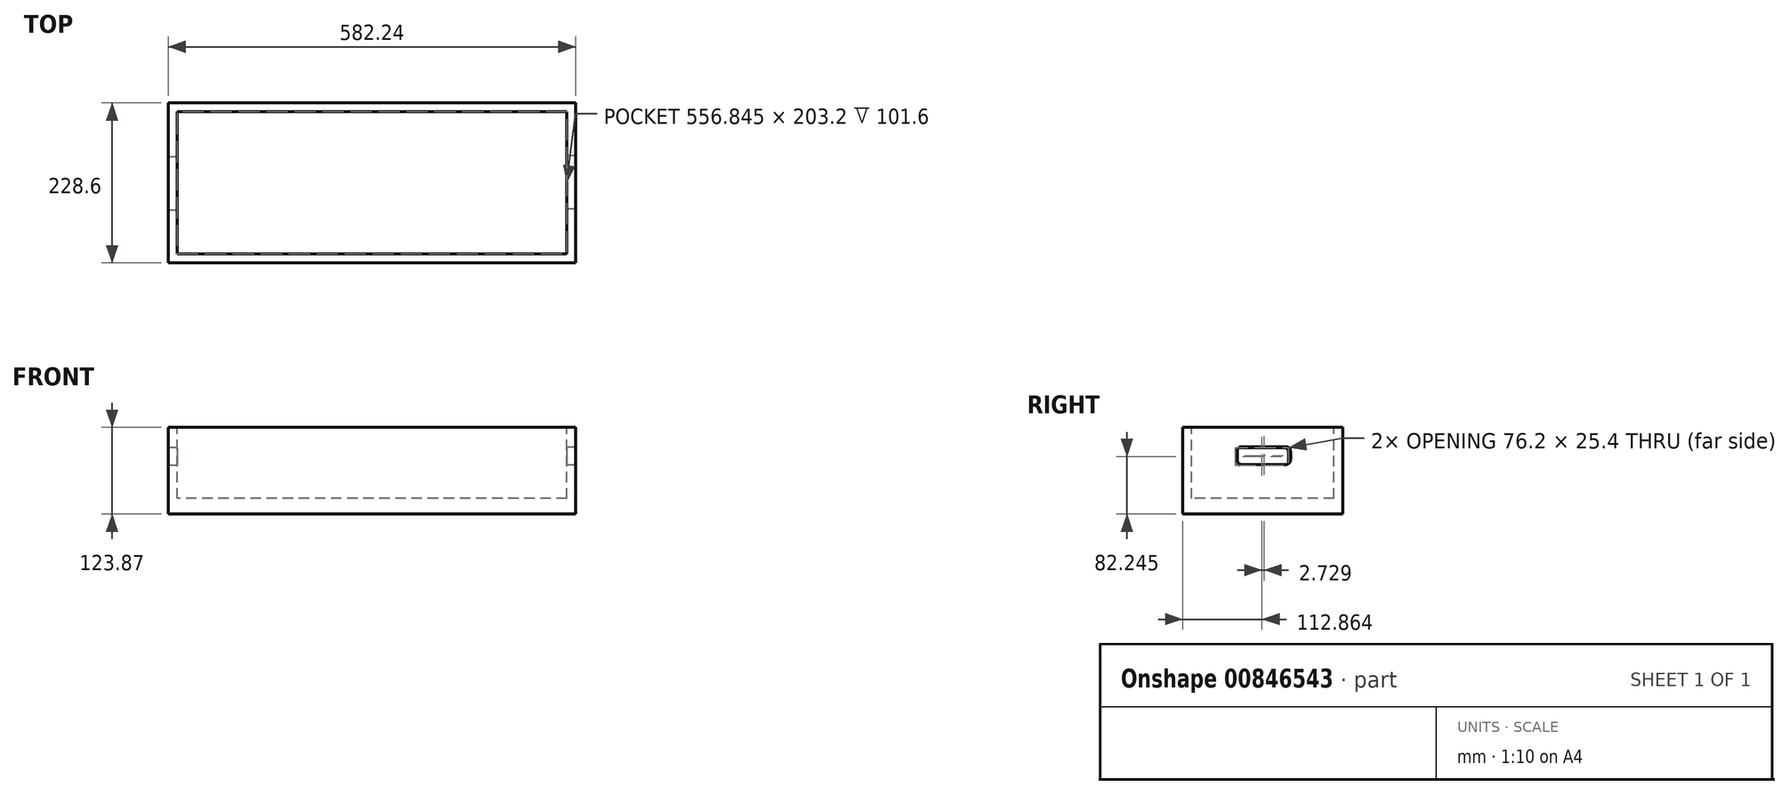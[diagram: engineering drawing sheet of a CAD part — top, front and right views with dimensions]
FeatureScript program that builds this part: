
annotation { "Feature Type Name" : "Feature", "Feature Type Description" : "" }
export const myFeature = defineFeature(function(context is Context, id is Id, definition is map)
    precondition{}
    {
        {
            var Q0;
            Q0=qCreatedBy(makeId("Front.planeOp"),FACE);
            var sketch = newSketch(context, id + "F0", { "sketchPlane" : qUnion([Q0])});
            skLineSegment(sketch, "E0.bottom", {"start": v(-103.31, 21.1) * mm, "end": v(478.93, 21.1) * mm});
            skLineSegment(sketch, "E0.top", {"start": v(-103.31, -102.77) * mm, "end": v(478.93, -102.77) * mm});
            skLineSegment(sketch, "E0.left", {"start": v(-103.31, 21.1) * mm, "end": v(-103.31, -102.77) * mm});
            skLineSegment(sketch, "E0.right", {"start": v(478.93, 21.1) * mm, "end": v(478.93, -102.77) * mm});
            skSolve(sketch);
        }
        {
            var Q0;
            Q0 = qSketchRegion(id + "F0", true);
            extrude(context, id + "F1", {"entities" : qUnion([Q0]), "depth" : 228.6 * mm, "offsetDistance" : 25 * mm});
        }
        {
            var Q0;
            Q0=makeQuery(id+"F1.opExtrude","SWEPT_FACE",FACE,{"disambiguationData":[OSD([sQuery(id+"F0.wireOp",EDGE,"E0.bottom")])]});
            var sketch = newSketch(context, id + "F2", { "sketchPlane" : qUnion([Q0])});
            skLineSegment(sketch, "E1.0", {"start": v(466.23, -12.7) * mm, "end": v(-90.61, -12.7) * mm});
            skLineSegment(sketch, "E1.1", {"start": v(466.23, -215.9) * mm, "end": v(466.23, -12.7) * mm});
            skLineSegment(sketch, "E1.2", {"start": v(-90.61, -215.9) * mm, "end": v(466.23, -215.9) * mm});
            skLineSegment(sketch, "E1.3", {"start": v(-90.61, -12.7) * mm, "end": v(-90.61, -215.9) * mm});
            skLineSegment(sketch, "E2.0", {"start": v(472.75, -6.18) * mm, "end": v(-97.13, -6.18) * mm});
            skLineSegment(sketch, "E2.1", {"start": v(472.75, -222.42) * mm, "end": v(472.75, -6.18) * mm});
            skLineSegment(sketch, "E2.2", {"start": v(-97.13, -222.42) * mm, "end": v(472.75, -222.42) * mm});
            skLineSegment(sketch, "E2.3", {"start": v(-97.13, -6.18) * mm, "end": v(-97.13, -222.42) * mm});
            skSolve(sketch);
        }
        {
            var Q0;
            Q0=makeQuery(id+"F2.imprint","IMPRINT",FACE,{"disambiguationData":[TD([[makeQuery(id+"F2.imprint","IMPRINT",EDGE,{"derivedFrom":sQuery(id+"F2.wireOp",EDGE,"E1.0")}),1.0]])]});
            extrude(context, id + "F3", {"entities" : qUnion([Q0]), "operationType" : NewBodyOperationType.REMOVE, "oppositeDirection" : true, "depth" : 101.6 * mm, "offsetDistance" : 25.4 * mm});
        }
        {
            var Q0;
            Q0=makeQuery(id+"F1.opExtrude","SWEPT_FACE",FACE,{"disambiguationData":[OSD([sQuery(id+"F0.wireOp",EDGE,"E0.right")])]});
            var sketch = newSketch(context, id + "F4", { "sketchPlane" : qUnion([Q0])});
            skLineSegment(sketch, "E3.bottom", {"start": v(-144.76, -6.45) * mm, "end": v(-81.26, -6.45) * mm});
            skLineSegment(sketch, "E3.top", {"start": v(-144.76, -31.85) * mm, "end": v(-81.26, -31.85) * mm});
            skLineSegment(sketch, "E3.left", {"start": v(-151.1, -12.8) * mm, "end": v(-151.1, -25.5) * mm});
            skLineSegment(sketch, "E3.right", {"start": v(-74.9, -12.8) * mm, "end": v(-74.9, -25.5) * mm});
            skPoint(sketch, "E4.visualSharp", {"position": v(-151.1, -6.45) * mm});
            skArc(sketch, "E4.filletArc", {"start": v(-144.76, -6.45) * mm, "mid": v(-149.25, -8.3) * mm, "end": v(-151.1, -12.8) * mm});
            skPoint(sketch, "E5.visualSharp", {"position": v(-151.1, -31.85) * mm});
            skArc(sketch, "E5.filletArc", {"start": v(-151.1, -25.5) * mm, "mid": v(-149.25, -30) * mm, "end": v(-144.76, -31.85) * mm});
            skPoint(sketch, "E6.visualSharp", {"position": v(-74.9, -6.45) * mm});
            skArc(sketch, "E6.filletArc", {"start": v(-74.9, -12.8) * mm, "mid": v(-76.77, -8.3) * mm, "end": v(-81.26, -6.45) * mm});
            skPoint(sketch, "E7.visualSharp", {"position": v(-74.9, -31.85) * mm});
            skArc(sketch, "E7.filletArc", {"start": v(-81.26, -31.85) * mm, "mid": v(-76.77, -30) * mm, "end": v(-74.9, -25.5) * mm});
            skSolve(sketch);
        }
        {
            var Q0;
            Q0=makeQuery(id+"F4.imprint","IMPRINT",FACE,{"disambiguationData":[TD([[makeQuery(id+"F4.imprint","IMPRINT",EDGE,{"derivedFrom":sQuery(id+"F4.wireOp",EDGE,"E3.bottom")}),-1.0]])]});
            extrude(context, id + "F5", {"entities" : qUnion([Q0]), "operationType" : NewBodyOperationType.REMOVE, "oppositeDirection" : true, "depth" : 25.4 * mm, "offsetDistance" : 25.4 * mm});
        }
        {
            var Q0;
            Q0=makeQuery(id+"F1.opExtrude","SWEPT_FACE",FACE,{"disambiguationData":[OSD([sQuery(id+"F0.wireOp",EDGE,"E0.left")])]});
            var sketch = newSketch(context, id + "F6", { "sketchPlane" : qUnion([Q0])});
            skLineSegment(sketch, "E8.bottom", {"start": v(83.99, -7.83) * mm, "end": v(147.49, -7.83) * mm});
            skLineSegment(sketch, "E8.top", {"start": v(83.99, -33.23) * mm, "end": v(147.49, -33.23) * mm});
            skLineSegment(sketch, "E8.left", {"start": v(77.64, -14.18) * mm, "end": v(77.64, -26.88) * mm});
            skLineSegment(sketch, "E8.right", {"start": v(153.84, -14.18) * mm, "end": v(153.84, -26.88) * mm});
            skPoint(sketch, "E9.visualSharp", {"position": v(77.64, -7.83) * mm});
            skArc(sketch, "E9.filletArc", {"start": v(83.99, -7.83) * mm, "mid": v(79.5, -9.68) * mm, "end": v(77.64, -14.18) * mm});
            skPoint(sketch, "E10.visualSharp", {"position": v(77.64, -33.23) * mm});
            skArc(sketch, "E10.filletArc", {"start": v(77.64, -26.88) * mm, "mid": v(79.5, -31.37) * mm, "end": v(83.99, -33.23) * mm});
            skPoint(sketch, "E11.visualSharp", {"position": v(153.84, -7.83) * mm});
            skArc(sketch, "E11.filletArc", {"start": v(153.84, -14.18) * mm, "mid": v(151.98, -9.68) * mm, "end": v(147.49, -7.83) * mm});
            skPoint(sketch, "E12.visualSharp", {"position": v(153.84, -33.23) * mm});
            skArc(sketch, "E12.filletArc", {"start": v(147.49, -33.23) * mm, "mid": v(151.98, -31.37) * mm, "end": v(153.84, -26.88) * mm});
            skSolve(sketch);
        }
        {
            var Q0;
            Q0=makeQuery(id+"F6.imprint","IMPRINT",FACE,{"disambiguationData":[TD([[makeQuery(id+"F6.imprint","IMPRINT",EDGE,{"derivedFrom":sQuery(id+"F6.wireOp",EDGE,"E8.bottom")}),-1.0]])]});
            extrude(context, id + "F7", {"entities" : qUnion([Q0]), "operationType" : NewBodyOperationType.REMOVE, "oppositeDirection" : true, "depth" : 25.4 * mm, "offsetDistance" : 25.4 * mm});
        }
    });
